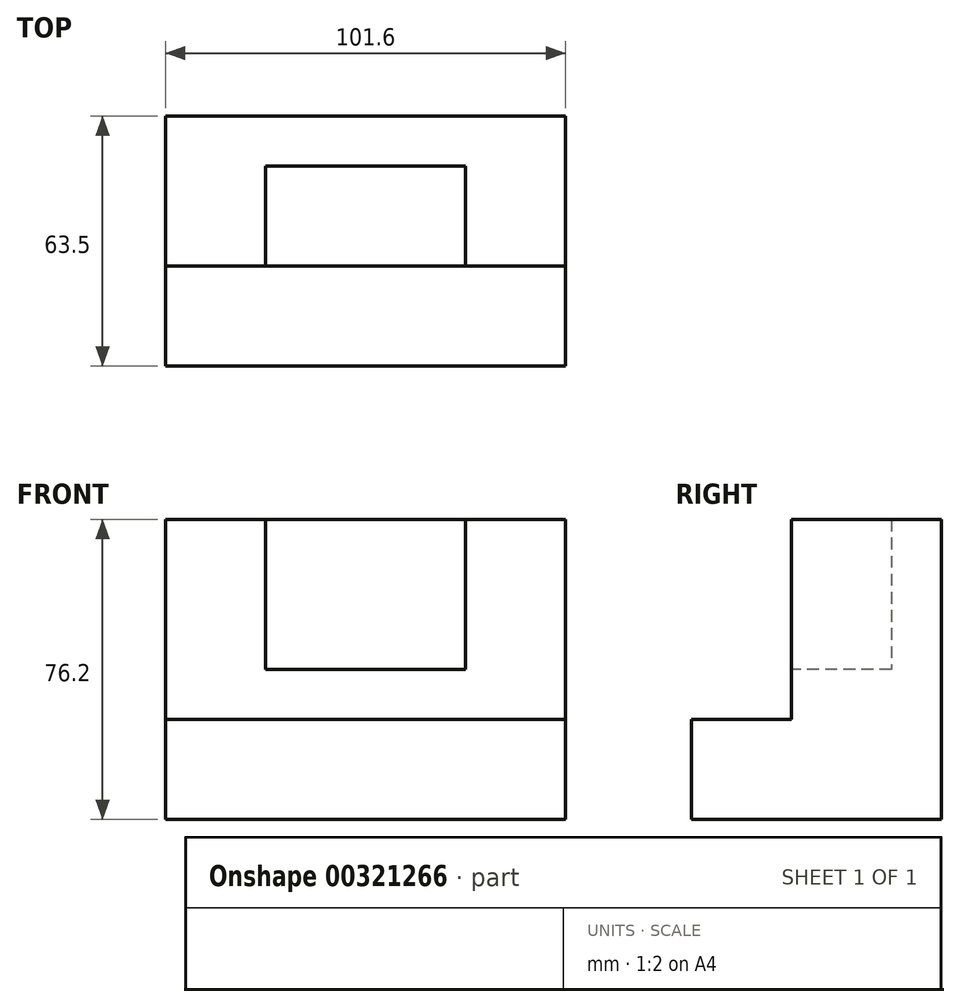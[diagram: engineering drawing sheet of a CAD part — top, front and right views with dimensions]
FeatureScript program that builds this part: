
annotation { "Feature Type Name" : "Feature", "Feature Type Description" : "" }
export const myFeature = defineFeature(function(context is Context, id is Id, definition is map)
    precondition{}
    {
        {
            var Q0;
            Q0=qCreatedBy(makeId("Right.planeOp"),FACE);
            var sketch = newSketch(context, id + "F0", { "sketchPlane" : qUnion([Q0])});
            skLineSegment(sketch, "E0", {"start": v(-23.99, -25.37) * mm, "end": v(39.51, -25.37) * mm});
            skLineSegment(sketch, "E1", {"start": v(39.51, -25.37) * mm, "end": v(39.51, 50.83) * mm});
            skLineSegment(sketch, "E2", {"start": v(39.51, 50.83) * mm, "end": v(1.41, 50.83) * mm});
            skLineSegment(sketch, "E3", {"start": v(1.41, 50.83) * mm, "end": v(1.41, 0.03) * mm});
            skLineSegment(sketch, "E4", {"start": v(1.41, 0.03) * mm, "end": v(-23.99, 0.03) * mm});
            skLineSegment(sketch, "E5", {"start": v(-23.99, 0.03) * mm, "end": v(-23.99, -25.37) * mm});
            skSolve(sketch);
        }
        {
            var Q0;
            Q0 = qSketchRegion(id + "F0", true);
            extrude(context, id + "F1", {"entities" : qUnion([Q0]), "depth" : 101.6 * mm});
        }
        {
            var Q0;
            Q0=makeQuery(id+"F1.opExtrude","SWEPT_FACE",FACE,{"disambiguationData":[OSD([sQuery(id+"F0.wireOp",EDGE,"E3")])]});
            var sketch = newSketch(context, id + "F2", { "sketchPlane" : qUnion([Q0])});
            skLineSegment(sketch, "E6.bottom", {"start": v(25.4, 50.83) * mm, "end": v(76.2, 50.83) * mm});
            skLineSegment(sketch, "E6.top", {"start": v(25.4, 12.73) * mm, "end": v(76.2, 12.73) * mm});
            skLineSegment(sketch, "E6.left", {"start": v(25.4, 50.83) * mm, "end": v(25.4, 12.73) * mm});
            skLineSegment(sketch, "E6.right", {"start": v(76.2, 50.83) * mm, "end": v(76.2, 12.73) * mm});
            skSolve(sketch);
        }
        {
            var Q0;
            Q0 = qSketchRegion(id + "F2", true);
            extrude(context, id + "F3", {"entities" : qUnion([Q0]), "operationType" : NewBodyOperationType.REMOVE, "oppositeDirection" : true, "depth" : 25.4 * mm});
        }
    });
